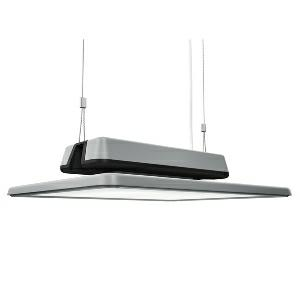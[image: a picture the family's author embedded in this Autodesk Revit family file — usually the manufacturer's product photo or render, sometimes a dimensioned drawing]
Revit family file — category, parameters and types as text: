
# Revit family: acaneo_-_hial_30000_850_w_dali_00733709_c6f6
name_source: partatom
category: Lighting Fixtures
units: mm (PartAtom-declared; Revit-internal decimal feet)

## family parameters
Cut with Voids When Loaded = No
Host = Face
Light Source = No
Part Type = Normal
Room Calculation Point = No
Round Connector Dimension = Use Diameter
Shared = No

## types (1)
- ACANEO - HIAL 30000/850/W/DALI (1 x LED, 33000 lm, 5000K)
    Apparent Load = 206 VA
    Approval mark = CE
    CIE Flux Codes = 76 97 99 100 100
    Color Rendering = 80-89
    Color Temperature = 5000K
    Control Gear = Electronic ballast
    Default Elevation = 1800 mm
    Description = HIAL 30000/850/W/DALI|High bay luminaire|light source: LED|work equipment: Adjustable electronic ballast, digital DALI|connected load: 220-240 V, 50/60 Hz|Power consumption: approx. 206 W|power factor: approx. 0,973|luminous flux: 33000 lm|luminous efficacy: 160 lm/W|colour temperature: Cold white, ca. 5000 K|color rendering index (CRI): >= 80|chromaticity tolerance:  3 SDCM|System of protection: IP 65|class of protection: I|technology: Continuously dimmable|luminaire body|material: Aluminium|surface: Powder coatet|colour: White aluminium|lamp cover: Acrylic (PMMA), Clear|weight (net): approx. 10.8 kg|mains lead: Built-in plug RST 20i5 Einbau|Fastening: Available separately|Accessory: Junction box (RST 20i5)|minimum ambient temperature: -30 ░C|maximum ambient temperature: 60 ░C|glare control: Optics|unified glare rating(4H 8H): <=  25|
    Frequency = 50 Hz, 60 Hz
    Height = 125 mm
    Lamp = 1 x LED
    Lamp Light Flux = 33000 lm
    Lamp count = 1
    Length = 585 mm
    Luminous efficacy = 160 lm/W
    Manufacturer = Waldmann
    ModVariant = No
    Model = 00733709
    Mounting Place = Ceiling
    Mounting Type = Pendant
    Number of Poles = 1
    OnlyDefault = Yes
    Power Factor = 1
    Product Name = ACANEO - HIAL 30000/850/W/DALI
    Product group = High bay luminaire (industry)
    ProductGroupID = 901
    Protection Class = Protection class I
    Protection Degree = IP 65
    RLX_Detail_Level = 1
    RLX_Emergency_Light_Flux = 0 lm
    RLX_Emergency_Type = 0
    RLX_Emergency_Type_DB = No
    RlxData = <blob elided: 30005 chars, md5=71c49f22>
    Socket = socket
    Standby Power = 0 W
    System Light Flux = 32999 lm
    System Power = 206 W
    Type Comments = Product without accessories
    Type Image = acaneo-hial.jpg
    URL = http://relux.com
    VarID = ---
    Voltage = 230 V
    Voltage Range = 110-120 V, 220-240 V
    Weight = 0.00 kg
    Width = 480 mm

## geometry (parser evidence)
native form markers: Blend x4, Sweep x11
no freeform markers — native parametric forms only
